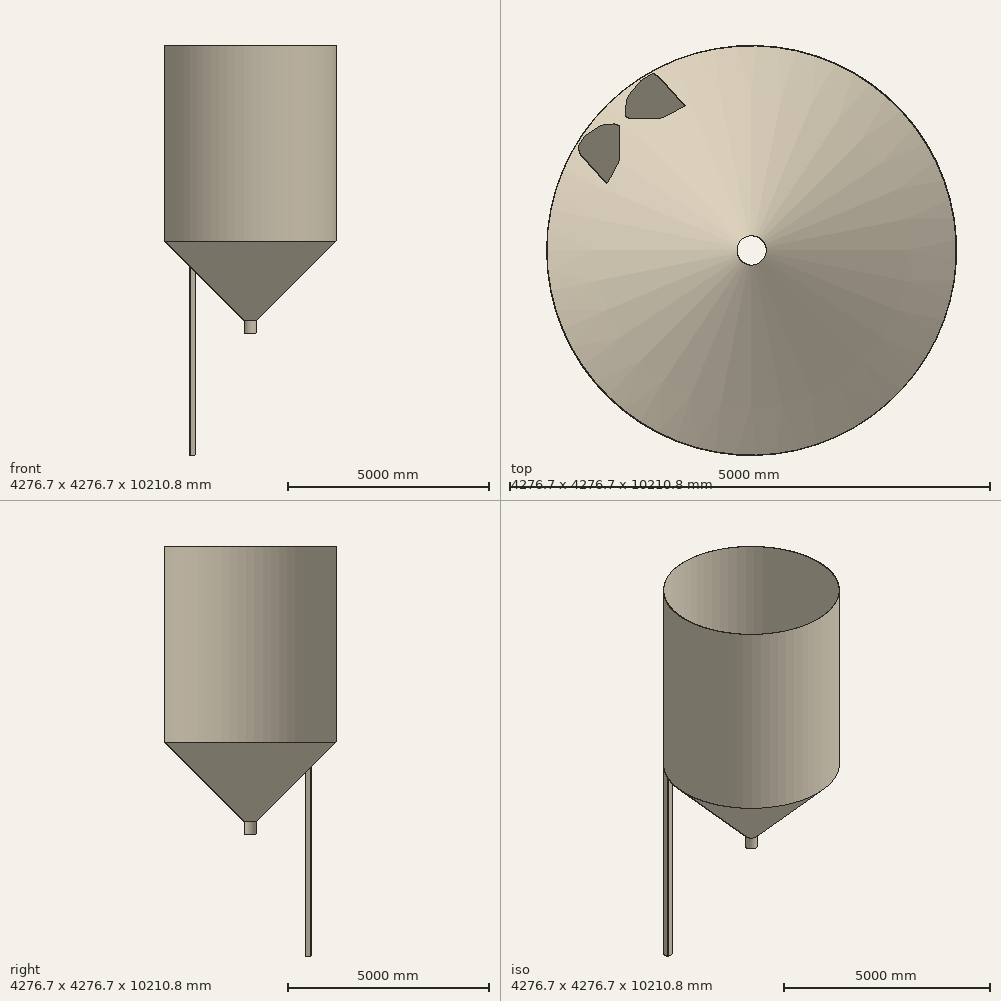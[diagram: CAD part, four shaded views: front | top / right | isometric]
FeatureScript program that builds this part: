
annotation { "Feature Type Name" : "Feature", "Feature Type Description" : "" }
export const myFeature = defineFeature(function(context is Context, id is Id, definition is map)
    precondition{}
    {
        {
            var Q0;
            Q0=qCreatedBy(makeId("Front.planeOp"),FACE);
            var sketch = newSketch(context, id + "F0", { "sketchPlane" : qUnion([Q0])});
            skLineSegment(sketch, "E0", {"start": v(0, 0) * mm, "end": v(0, 2087.68) * mm, "construction": true});
            skLineSegment(sketch, "E1", {"start": v(0, 0) * mm, "end": v(2133.6, 0) * mm, "construction": true});
            skLineSegment(sketch, "E2", {"start": v(152.4, -1981.2) * mm, "end": v(2133.6, 0) * mm});
            skLineSegment(sketch, "E3", {"start": v(2133.6, 4876.8) * mm, "end": v(2133.6, 0) * mm});
            skLineSegment(sketch, "E4", {"start": v(152.4, -1981.2) * mm, "end": v(152.4, -2286) * mm});
            skLineSegment(sketch, "E5", {"start": v(0, 0) * mm, "end": v(0, -1981.2) * mm, "construction": true});
            skLineSegment(sketch, "E6", {"start": v(0, -1981.2) * mm, "end": v(1823.7, -1981.2) * mm, "construction": true});
            skLineSegment(sketch, "E7.0", {"start": v(157.16, -1983.17) * mm, "end": v(157.16, -2286) * mm});
            skLineSegment(sketch, "E7.1", {"start": v(157.16, -1983.17) * mm, "end": v(2138.36, -1.97) * mm});
            skLineSegment(sketch, "E7.2", {"start": v(2138.36, 4876.8) * mm, "end": v(2138.36, -1.97) * mm});
            skLineSegment(sketch, "E8", {"start": v(152.4, -2286) * mm, "end": v(157.16, -2286) * mm});
            skLineSegment(sketch, "E9", {"start": v(2133.6, 4876.8) * mm, "end": v(2138.36, 4876.8) * mm});
            skSolve(sketch);
        }
        {
            var Q0;
            Q0=qSketchRegion(id+"F0",true);
            var Q1;
            Q1=sQuery(id+"F0.wireOp",EDGE,"E0");
            revolve(context, id + "F1", {"entities" : qUnion([Q0]), "axis" : qUnion([Q1]), "revolveType" : RevolveType.FULL});
        }
        {
            var Q0;
            Q0=qCreatedBy(makeId("Top.planeOp"),FACE);
            cPlane(context, id + "F2", {"entities" : qUnion([Q0]), "cplaneType" : CPlaneType.OFFSET, "offset" : 5334 * mm, "oppositeDirection" : true, "width" : 152.4 * mm, "height" : 152.4 * mm});
        }
        {
            var Q0;
            Q0=qCreatedBy(id+"F2.planeOp",FACE);
            var sketch = newSketch(context, id + "F3", { "sketchPlane" : qUnion([Q0])});
            skLineSegment(sketch, "E10.bottom", {"start": v(-1512.05, -1512.05) * mm, "end": v(1512.05, -1512.05) * mm, "construction": true});
            skLineSegment(sketch, "E10.top", {"start": v(-1512.05, 1512.05) * mm, "end": v(1512.05, 1512.05) * mm, "construction": true});
            skLineSegment(sketch, "E10.left", {"start": v(-1512.05, -1512.05) * mm, "end": v(-1512.05, 1512.05) * mm, "construction": true});
            skLineSegment(sketch, "E10.right", {"start": v(1512.05, -1512.05) * mm, "end": v(1512.05, 1512.05) * mm, "construction": true});
            skPoint(sketch, "E10.middle", {"position": v(0, 0) * mm});
            skLineSegment(sketch, "E11.bottom", {"start": v(-1499.35, 1512.05) * mm, "end": v(-1372.35, 1512.05) * mm});
            skLineSegment(sketch, "E11.top", {"start": v(-1499.35, 1359.65) * mm, "end": v(-1372.35, 1359.65) * mm});
            skLineSegment(sketch, "E11.left", {"start": v(-1512.05, 1499.35) * mm, "end": v(-1512.05, 1372.35) * mm});
            skLineSegment(sketch, "E11.right", {"start": v(-1359.65, 1499.35) * mm, "end": v(-1359.65, 1372.35) * mm});
            skLineSegment(sketch, "E12.0", {"start": v(-1505.7, 1493) * mm, "end": v(-1505.7, 1378.7) * mm});
            skLineSegment(sketch, "E12.1", {"start": v(-1493, 1505.7) * mm, "end": v(-1378.7, 1505.7) * mm});
            skLineSegment(sketch, "E12.2", {"start": v(-1366, 1493) * mm, "end": v(-1366, 1378.7) * mm});
            skLineSegment(sketch, "E12.3", {"start": v(-1493, 1366) * mm, "end": v(-1378.7, 1366) * mm});
            skPoint(sketch, "E13.visualSharp", {"position": v(-1505.7, 1366) * mm});
            skArc(sketch, "E13.filletArc", {"start": v(-1505.7, 1378.7) * mm, "mid": v(-1501.98, 1369.72) * mm, "end": v(-1493, 1366) * mm});
            skPoint(sketch, "E14.visualSharp", {"position": v(-1512.05, 1359.65) * mm});
            skArc(sketch, "E14.filletArc", {"start": v(-1512.05, 1372.35) * mm, "mid": v(-1508.33, 1363.37) * mm, "end": v(-1499.35, 1359.65) * mm});
            skPoint(sketch, "E15.visualSharp", {"position": v(-1366, 1366) * mm});
            skArc(sketch, "E15.filletArc", {"start": v(-1378.7, 1366) * mm, "mid": v(-1369.72, 1369.72) * mm, "end": v(-1366, 1378.7) * mm});
            skPoint(sketch, "E16.visualSharp", {"position": v(-1359.65, 1359.65) * mm});
            skArc(sketch, "E16.filletArc", {"start": v(-1372.35, 1359.65) * mm, "mid": v(-1363.37, 1363.37) * mm, "end": v(-1359.65, 1372.35) * mm});
            skPoint(sketch, "E17.visualSharp", {"position": v(-1359.65, 1512.05) * mm});
            skArc(sketch, "E17.filletArc", {"start": v(-1359.65, 1499.35) * mm, "mid": v(-1363.37, 1508.33) * mm, "end": v(-1372.35, 1512.05) * mm});
            skPoint(sketch, "E18.visualSharp", {"position": v(-1505.7, 1505.7) * mm});
            skArc(sketch, "E18.filletArc", {"start": v(-1493, 1505.7) * mm, "mid": v(-1501.98, 1501.98) * mm, "end": v(-1505.7, 1493) * mm});
            skPoint(sketch, "E19.visualSharp", {"position": v(-1512.05, 1512.05) * mm});
            skArc(sketch, "E19.filletArc", {"start": v(-1499.35, 1512.05) * mm, "mid": v(-1508.33, 1508.33) * mm, "end": v(-1512.05, 1499.35) * mm});
            skPoint(sketch, "E20.visualSharp", {"position": v(-1366, 1505.7) * mm});
            skArc(sketch, "E20.filletArc", {"start": v(-1366, 1493) * mm, "mid": v(-1369.72, 1501.98) * mm, "end": v(-1378.7, 1505.7) * mm});
            skSolve(sketch);
        }
        {
            var Q0;
            Q0=qSketchRegion(id+"F3",true);
            var Q1;
            Q1=makeQuery(id+"F1.opRevolve","SWEPT_FACE",FACE,{"disambiguationData":[OSD([sQuery(id+"F0.wireOp",EDGE,"E7.1")])]});
            extrude(context, id + "F4", {"entities" : qUnion([Q0]), "operationType" : NewBodyOperationType.ADD, "endBound" : BoundingType.UP_TO_SURFACE, "endBoundEntityFace" : qUnion([Q1]), "depth" : 25.4 * mm});
        }
        {
            var Q0;
            Q0=makeQuery(id+"FP6Go0r2yN7Bhfs_1.2.F4.opExtrude","CAP_FACE",FACE,{"disambiguationData":[OSD([sQuery(id+"F3.wireOp",EDGE,"E11.bottom"),sQuery(id+"F3.wireOp",EDGE,"E11.top"),sQuery(id+"F3.wireOp",EDGE,"E11.left"),sQuery(id+"F3.wireOp",EDGE,"E11.right"),sQuery(id+"F3.wireOp",EDGE,"E12.0"),sQuery(id+"F3.wireOp",EDGE,"E12.1"),sQuery(id+"F3.wireOp",EDGE,"E12.2"),sQuery(id+"F3.wireOp",EDGE,"E12.3"),sQuery(id+"F3.wireOp",EDGE,"E13.filletArc"),sQuery(id+"F3.wireOp",EDGE,"E14.filletArc"),sQuery(id+"F3.wireOp",EDGE,"E15.filletArc"),sQuery(id+"F3.wireOp",EDGE,"E16.filletArc"),sQuery(id+"F3.wireOp",EDGE,"E17.filletArc"),sQuery(id+"F3.wireOp",EDGE,"E18.filletArc"),sQuery(id+"F3.wireOp",EDGE,"E19.filletArc"),sQuery(id+"F3.wireOp",EDGE,"E20.filletArc")])],"isStart":true});
            var sketch = newSketch(context, id + "F5", { "sketchPlane" : qUnion([Q0])});
            skPoint(sketch, "E21.startSnap0", {"position": v(-1508.33, 1508.33) * mm});
            skLineSegment(sketch, "E22", {"start": v(-1508.33, 1508.33) * mm, "end": v(-1381.33, 1381.33) * mm, "construction": true});
            skLineSegment(sketch, "E23", {"start": v(-1444.83, 1444.83) * mm, "end": v(0, 2030.6) * mm, "construction": true});
            skLineSegment(sketch, "E24", {"start": v(0, 2133.1) * mm, "end": v(0, 1928.1) * mm, "construction": true});
            skSolve(sketch);
        }
    });
